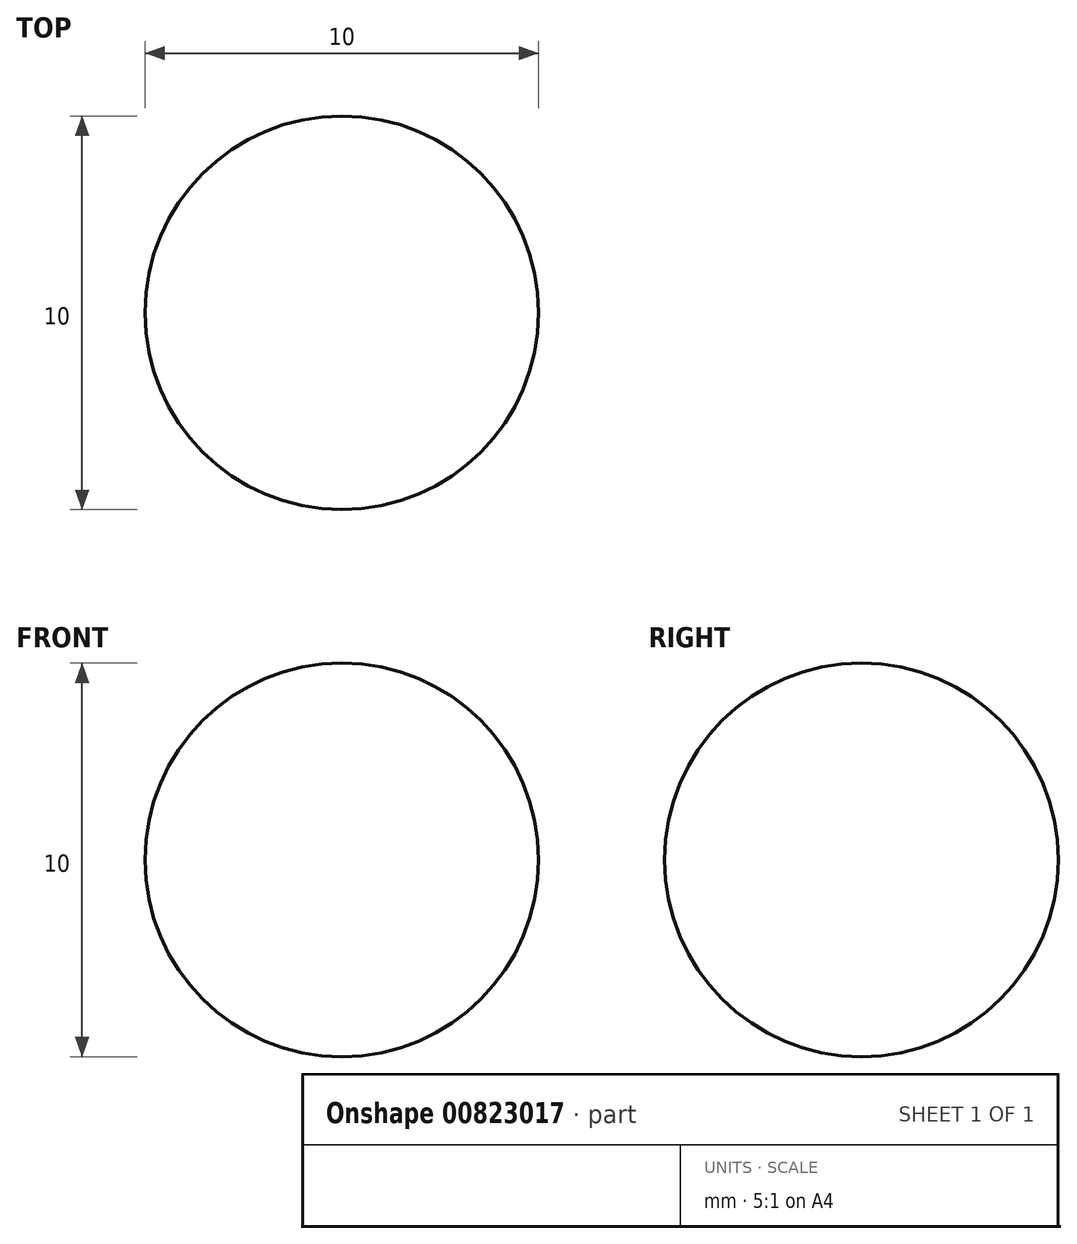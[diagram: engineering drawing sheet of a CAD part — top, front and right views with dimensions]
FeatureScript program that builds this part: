
annotation { "Feature Type Name" : "Feature", "Feature Type Description" : "" }
export const myFeature = defineFeature(function(context is Context, id is Id, definition is map)
    precondition{}
    {
        {
            var Q0;
            Q0=qCreatedBy(makeId("Front.planeOp"),FACE);
            var sketch = newSketch(context, id + "F0", { "sketchPlane" : qUnion([Q0])});
            skArc(sketch, "E0", {"start": v(5, 0) * mm, "mid": v(0, 5) * mm, "end": v(-5, 0) * mm});
            skLineSegment(sketch, "E1", {"start": v(-5, 0) * mm, "end": v(5, 0) * mm});
            skLineSegment(sketch, "E2", {"start": v(5, 0) * mm, "end": v(10.67, 0) * mm, "construction": true});
            skSolve(sketch);
        }
        {
            var Q0;
            Q0 = qSketchRegion(id + "F0", true);
            var Q1;
            Q1=sQuery(id+"F0.wireOp",EDGE,"E2");
            revolve(context, id + "F1", {"surfaceOperationType" : NewSurfaceOperationType.NEW, "entities" : qUnion([Q0]), "axis" : qUnion([Q1]), "revolveType" : RevolveType.FULL});
        }
    });
